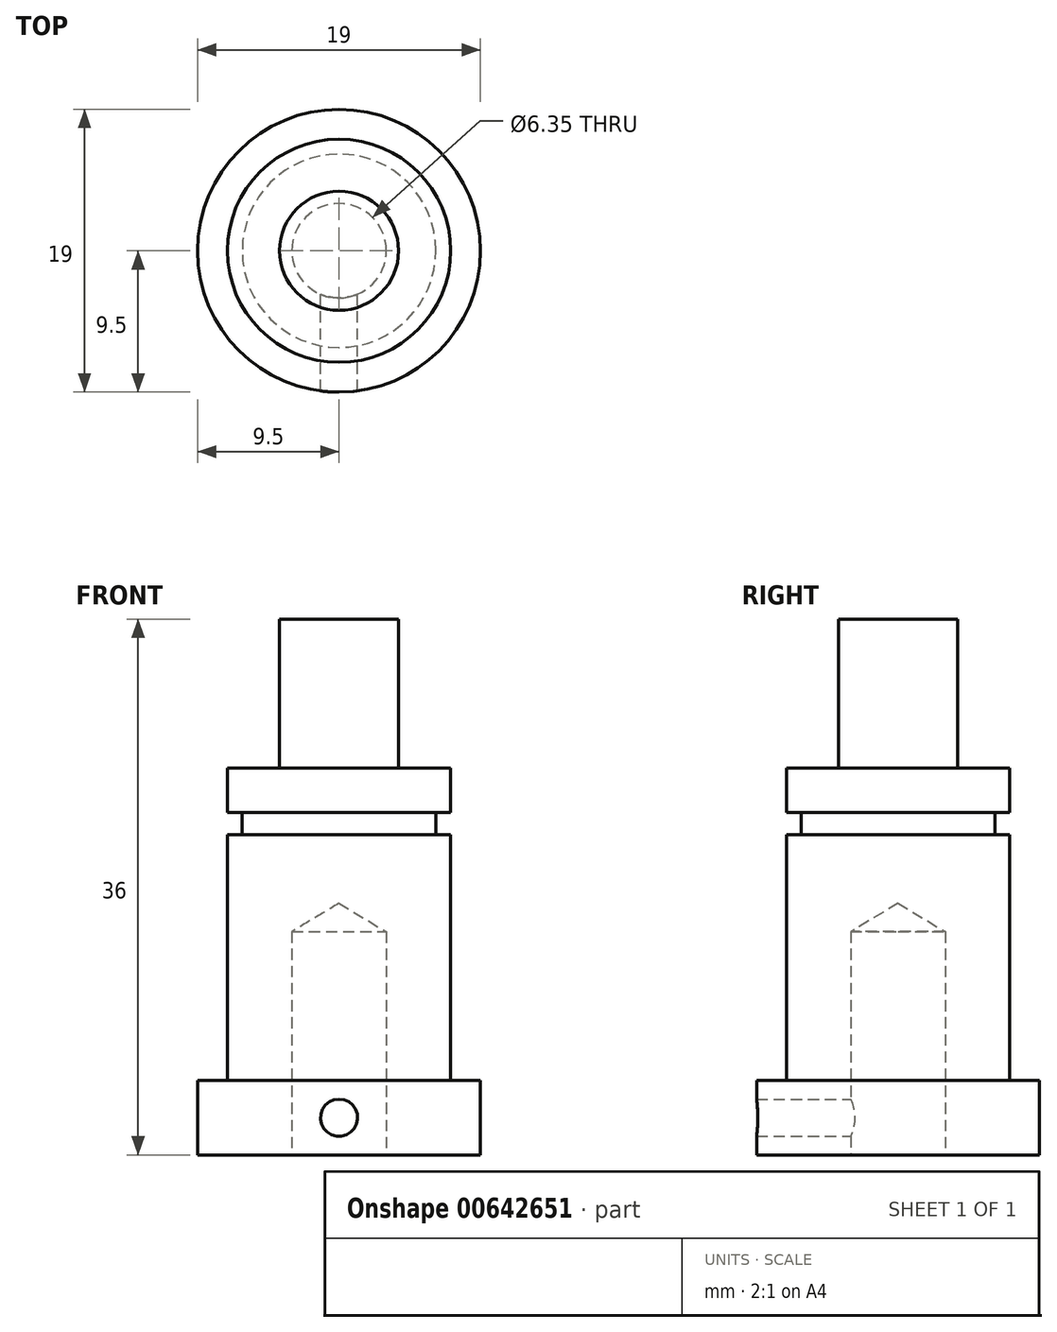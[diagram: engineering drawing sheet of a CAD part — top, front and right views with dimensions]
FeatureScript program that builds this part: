
annotation { "Feature Type Name" : "Feature", "Feature Type Description" : "" }
export const myFeature = defineFeature(function(context is Context, id is Id, definition is map)
    precondition{}
    {
        {
            var Q0;
            Q0=qCreatedBy(makeId("Top.planeOp"),FACE);
            var sketch = newSketch(context, id + "F0", { "sketchPlane" : qUnion([Q0])});
            skCircle(sketch, "E0", {"center": v(0, 0) * mm, "radius": 7.5 * mm});
            skSolve(sketch);
        }
        {
            var Q0;
            Q0=makeQuery(id+"F0.imprint","IMPRINT",FACE,{"disambiguationData":[TD([[makeQuery(id+"F0.imprint","IMPRINT",EDGE,{"derivedFrom":sQuery(id+"F0.wireOp",EDGE,"E0")}),1.0]])]});
            var Q1;
            Q1=sQuery(id+"F0.wireOp",EDGE,"7MQO46iF-WnG2-VvIN-YYpT-UoJq4p8WcKAx");
            var Q2;
            Q2=sQuery(id+"F0.wireOp",EDGE,"E0");
            extrude(context, id + "F1", {"entities" : qUnion([Q0]), "surfaceEntities" : qUnion([Q1, Q2]), "depth" : 21 * mm, "offsetDistance" : 25 * mm});
        }
        {
            var Q0;
            Q0=qCreatedBy(makeId("Top.planeOp"),FACE);
            var sketch = newSketch(context, id + "F2", { "sketchPlane" : qUnion([Q0])});
            skCircle(sketch, "E1", {"center": v(0, 0) * mm, "radius": 9.5 * mm});
            skSolve(sketch);
        }
        {
            var Q0;
            Q0=makeQuery(id+"F2.imprint","IMPRINT",FACE,{"disambiguationData":[TD([[makeQuery(id+"F2.imprint","IMPRINT",EDGE,{"derivedFrom":sQuery(id+"F2.wireOp",EDGE,"E1")}),1.0]])]});
            var Q1;
            Q1=sQuery(id+"F2.wireOp",EDGE,"E1");
            extrude(context, id + "F3", {"entities" : qUnion([Q0]), "operationType" : NewBodyOperationType.ADD, "surfaceEntities" : qUnion([Q1]), "depth" : 5 * mm, "offsetDistance" : 25 * mm});
        }
        {
            var Q0;
            Q0=qCreatedBy(makeId("Top.planeOp"),FACE);
            var sketch = newSketch(context, id + "F4", { "sketchPlane" : qUnion([Q0])});
            skCircle(sketch, "E2", {"center": v(0, 0) * mm, "radius": 3.18 * mm});
            skSolve(sketch);
        }
        {
            var Q0;
            Q0=sQuery(id+"F4.wireOp",VERTEX,"E2.center");
            var Q1;
            Q1=makeQuery(id+"F1.opExtrude","SWEPT_BODY",BODY,{"disambiguationData":[OSD([sQuery(id+"F0.wireOp",EDGE,"E0")])]});
            hole(context, id + "F5", {"style" : HoleStyle.SIMPLE, "endStyle" : HoleEndStyle.BLIND, "oppositeDirection" : true, "holeDiameter" : 6.35 * mm, "majorDiameter" : 5 * mm, "holeDepth" : 15 * mm, "isTappedThrough" : true, "tappedDepth" : 12 * mm, "tapClearance" : 3, "locations" : qUnion([Q0]), "scope" : qUnion([Q1])});
        }
        {
            var Q0;
            Q0=qCreatedBy(makeId("Front.planeOp"),FACE);
            var sketch = newSketch(context, id + "F6", { "sketchPlane" : qUnion([Q0])});
            skLineSegment(sketch, "E3", {"start": v(0, 0) * mm, "end": v(31.95, 0) * mm});
            skLineSegment(sketch, "E4.0", {"start": v(0, 2.5) * mm, "end": v(31.95, 2.5) * mm, "construction": true});
            skCircle(sketch, "E5", {"center": v(0, 2.5) * mm, "radius": 1.5 * mm});
            skSolve(sketch);
        }
        {
            var Q0;
            Q0=sQuery(id+"F6.wireOp",VERTEX,"E4.0.start");
            var Q1;
            Q1=makeQuery(id+"F1.opExtrude","SWEPT_BODY",BODY,{"disambiguationData":[OSD([sQuery(id+"F0.wireOp",EDGE,"E0")])]});
            hole(context, id + "F7", {"style" : HoleStyle.SIMPLE, "endStyle" : HoleEndStyle.THROUGH, "oppositeDirection" : true, "standardTappedOrClearance" : lookupTablePath({ "standard" : "ISO", "fit" : "Normal", "engagement" : "75%", "pitch" : "0.5 mm", "size" : "M3", "type" : "Tapped" }), "standardBlindInLast" : lookupTablePath({ "fit" : "Standard", "standard" : "ISO", "engagement" : "75%", "pitch" : "0.5 mm", "size" : "M3", "type" : "Tapped" }), "holeDiameter" : 2.5 * mm, "majorDiameter" : 3 * mm, "showTappedDepth" : true, "isTappedThrough" : true, "tappedDepth" : 12 * mm, "tapClearance" : 3, "locations" : qUnion([Q0]), "scope" : qUnion([Q1])});
        }
        {
            var Q0;
            Q0=makeQuery(id+"F1.opExtrude","CAP_FACE",FACE,{"disambiguationData":[OSD([sQuery(id+"F0.wireOp",EDGE,"E0")])],"isStart":false});
            var sketch = newSketch(context, id + "F8", { "sketchPlane" : qUnion([Q0])});
            skCircle(sketch, "E6", {"center": v(0, 0) * mm, "radius": 7.5 * mm});
            skSolve(sketch);
        }
        {
            var Q0;
            Q0=makeQuery(id+"F8.imprint","IMPRINT",FACE,{"disambiguationData":[TD([[makeQuery(id+"F8.imprint","IMPRINT",EDGE,{"derivedFrom":makeQuery(id+"F5.hole-0.boolean.opBoolean","INTERSECT",EDGE,{"derivedFrom":[makeQuery(id+"F1.opExtrude","CAP_FACE",FACE,{"disambiguationData":[OSD([sQuery(id+"F0.wireOp",EDGE,"E0")])],"isStart":false}),makeQuery(id+"F5.hole-0.opRevolve","SWEPT_FACE",FACE,{"disambiguationData":[OSD([sQuery(id+"F5.hole-0.sketch.wireOp",EDGE,"core_line_2")])]})]})}),-1.0]])]});
            var Q1;
            Q1=makeQuery(id+"F8.imprint","IMPRINT",FACE,{"disambiguationData":[TD([[makeQuery(id+"F8.imprint","IMPRINT",EDGE,{"derivedFrom":sQuery(id+"F8.wireOp",EDGE,"E6")}),1.0]])]});
            extrude(context, id + "F9", {"entities" : qUnion([Q0, Q1]), "operationType" : NewBodyOperationType.ADD, "depth" : 5 * mm, "offsetDistance" : 25 * mm});
        }
        {
            var Q0;
            Q0=makeQuery(id+"F9.opExtrude","CAP_FACE",FACE,{"disambiguationData":[OSD([sQuery(id+"F8.wireOp",EDGE,"E6")])],"isStart":false});
            var sketch = newSketch(context, id + "F10", { "sketchPlane" : qUnion([Q0])});
            skCircle(sketch, "E7", {"center": v(0, 0) * mm, "radius": 4 * mm});
            skSolve(sketch);
        }
        {
            var Q0;
            Q0 = qSketchRegion(id + "F10", true);
            extrude(context, id + "F11", {"entities" : qUnion([Q0]), "operationType" : NewBodyOperationType.ADD, "depth" : 10 * mm, "offsetDistance" : 25 * mm});
        }
        {
            var Q0;
            Q0=makeQuery(id+"F3.opExtrude","CAP_FACE",FACE,{"disambiguationData":[OSD([sQuery(id+"F2.wireOp",EDGE,"E1")])],"isStart":false});
            cPlane(context, id + "F12", {"entities" : qUnion([Q0]), "cplaneType" : CPlaneType.OFFSET, "offset" : 16.5 * mm, "width" : 150 * mm, "height" : 150 * mm});
        }
        {
            var Q0;
            Q0=qCreatedBy(id+"F12.planeOp",FACE);
            var sketch = newSketch(context, id + "F13", { "sketchPlane" : qUnion([Q0])});
            skCircle(sketch, "E8", {"center": v(0, 0) * mm, "radius": 6.5 * mm});
            skCircle(sketch, "E9.0", {"center": v(0, 0) * mm, "radius": 7.5 * mm});
            skSolve(sketch);
        }
        {
            var Q0;
            Q0 = qSketchRegion(id + "F13", true);
            extrude(context, id + "F14", {"entities" : qUnion([Q0]), "operationType" : NewBodyOperationType.REMOVE, "depth" : 1.5 * mm, "offsetDistance" : 25 * mm});
        }
    });
